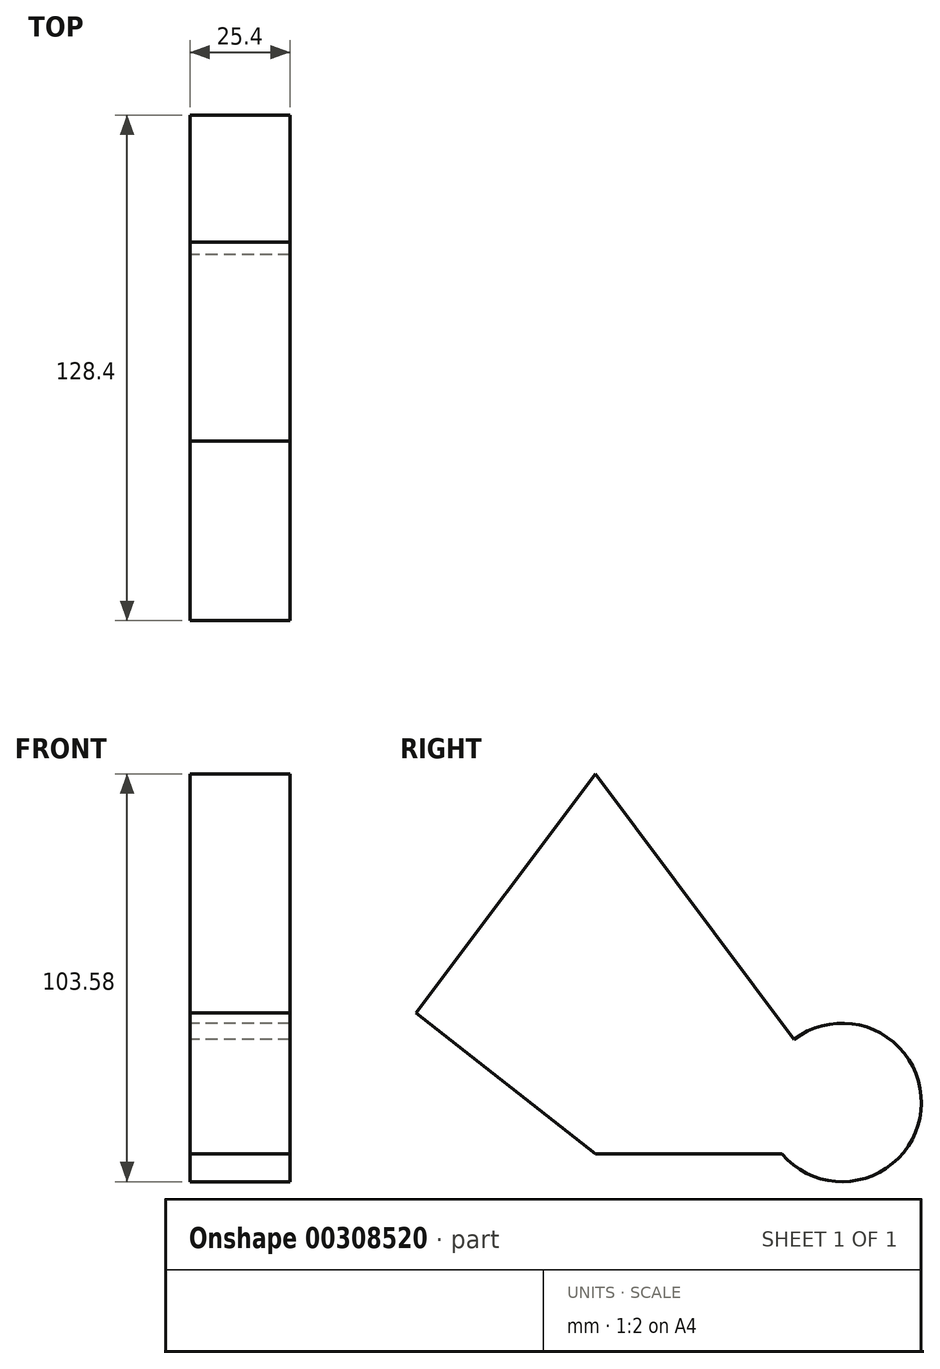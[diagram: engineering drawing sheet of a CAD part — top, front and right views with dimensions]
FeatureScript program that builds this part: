
annotation { "Feature Type Name" : "Feature", "Feature Type Description" : "" }
export const myFeature = defineFeature(function(context is Context, id is Id, definition is map)
    precondition{}
    {
        {
            var Q0;
            Q0=qCreatedBy(makeId("Right.planeOp"),FACE);
            var sketch = newSketch(context, id + "F0", { "sketchPlane" : qUnion([Q0])});
            skPoint(sketch, "E0.orphan", {"position": v(0, -85.79) * mm});
            skPoint(sketch, "E1.end.orphan", {"position": v(-111.47, -77.25) * mm});
            skPoint(sketch, "E2.top.start.orphan", {"position": v(-111.47, -61.44) * mm});
            skLineSegment(sketch, "E3", {"start": v(-108.28, 0) * mm, "end": v(-62.63, -35.8) * mm});
            skLineSegment(sketch, "E4", {"start": v(-62.63, -35.8) * mm, "end": v(-62.63, 60.75) * mm});
            skLineSegment(sketch, "E5", {"start": v(-62.63, 60.75) * mm, "end": v(-108.28, 0) * mm});
            skLineSegment(sketch, "E6", {"start": v(-62.63, -35.8) * mm, "end": v(9.55, -35.8) * mm});
            skLineSegment(sketch, "E7", {"start": v(9.55, -35.8) * mm, "end": v(-62.63, 60.75) * mm});
            skSolve(sketch);
        }
        {
            var Q0;
            Q0=makeQuery(id+"F0.imprint","IMPRINT",FACE,{"disambiguationData":[TD([[makeQuery(id+"F0.imprint","IMPRINT",EDGE,{"derivedFrom":sQuery(id+"F0.wireOp",EDGE,"E4")}),-1.0]])]});
            var Q1;
            Q1=makeQuery(id+"F0.imprint","IMPRINT",FACE,{"disambiguationData":[TD([[makeQuery(id+"F0.imprint","IMPRINT",EDGE,{"derivedFrom":sQuery(id+"F0.wireOp",EDGE,"E3")}),1.0]])]});
            extrude(context, id + "F1", {"entities" : qUnion([Q0, Q1]), "depth" : 25.4 * mm});
        }
        {
            var Q0;
            Q0=qCreatedBy(makeId("Right.planeOp"),FACE);
            var sketch = newSketch(context, id + "F2", { "sketchPlane" : qUnion([Q0])});
            skCircle(sketch, "E8", {"center": v(0, -22.7) * mm, "radius": 20.12 * mm});
            skSolve(sketch);
        }
        {
            var Q0;
            Q0 = qSketchRegion(id + "F2", true);
            extrude(context, id + "F3", {"entities" : qUnion([Q0]), "operationType" : NewBodyOperationType.ADD, "depth" : 25.4 * mm});
        }
    });
